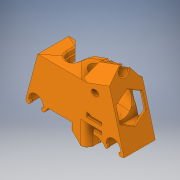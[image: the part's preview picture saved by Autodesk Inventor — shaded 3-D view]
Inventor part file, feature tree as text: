
AUTODESK INVENTOR PART (.ipt)
format: ipt  version: 2017 (Build 210142000, 142)  size: 1,958,912 bytes
history: native  units: in
note: dims shown in document units (in); Inventor stores cm internally (conversion verified against a paired STEP export)
features: other x1, fillet x1
ambient origin geometry x8: Origin, YZ Plane, XZ Plane, XY Plane, X Axis, Y Axis, Z Axis, Center Point
bodies: Solid1 (feature_tree)
feature tree (2):
  other  "14_tete.STEP"
  fillet  "Congé88"  [1 undecoded]
note: 1 required parameter value undecoded (feature->parameter linkage not recoverable at this tier; creation-order binding heuristic only, values carry confidence <= 0.55)
